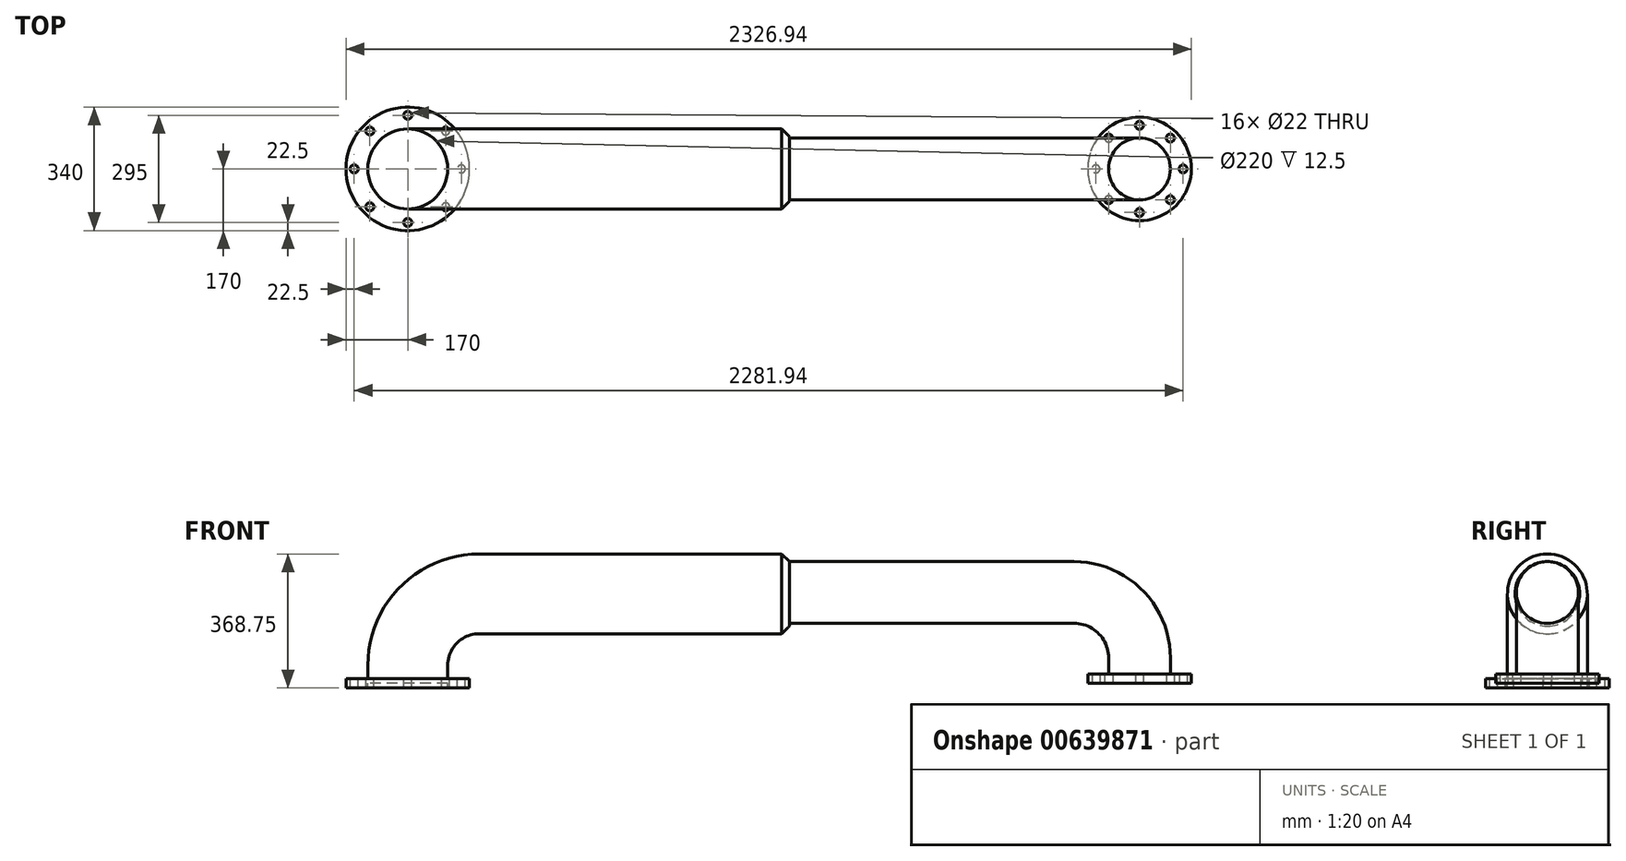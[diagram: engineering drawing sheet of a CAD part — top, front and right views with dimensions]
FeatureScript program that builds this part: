
annotation { "Feature Type Name" : "Feature", "Feature Type Description" : "" }
export const myFeature = defineFeature(function(context is Context, id is Id, definition is map)
    precondition{}
    {
        {
            var Q0;
            Q0=qCreatedBy(makeId("Top.planeOp"),FACE);
            var sketch = newSketch(context, id + "F0", { "sketchPlane" : qUnion([Q0])});
            skCircle(sketch, "E0", {"center": v(0, 0) * mm, "radius": 85 * mm});
            skSolve(sketch);
        }
        {
            var Q0;
            Q0=qCreatedBy(makeId("Front.planeOp"),FACE);
            var sketch = newSketch(context, id + "F1", { "sketchPlane" : qUnion([Q0])});
            skLineSegment(sketch, "E1", {"start": v(0, 0) * mm, "end": v(0, 70) * mm});
            skLineSegment(sketch, "E2", {"start": v(-180, 250) * mm, "end": v(-1000, 250) * mm});
            skPoint(sketch, "E3.visualSharp", {"position": v(0, 250) * mm});
            skArc(sketch, "E3.filletArc", {"start": v(0, 70) * mm, "mid": v(-52.72, 197.28) * mm, "end": v(-180, 250) * mm});
            skSolve(sketch);
        }
        {
            var Q0;
            Q0=makeQuery(id+"F0.imprint","IMPRINT",FACE,{"disambiguationData":[TD([[makeQuery(id+"F0.imprint","IMPRINT",EDGE,{"derivedFrom":sQuery(id+"F0.wireOp",EDGE,"E0")}),1.0]])]});
            var Q1;
            Q1=sQuery(id+"F1.wireOp",EDGE,"E1");
            var Q2;
            Q2=sQuery(id+"F1.wireOp",EDGE,"E3.filletArc");
            var Q3;
            Q3=sQuery(id+"F1.wireOp",EDGE,"E2");
            sweep(context, id + "F2", {"profiles" : qUnion([Q0]), "path" : qUnion([Q1, Q2, Q3])});
        }
        {
            var Q0;
            Q0=makeQuery(id+"F2.opSweep","CAP_FACE",FACE,{"disambiguationData":[OSD([sQuery(id+"F0.wireOp",EDGE,"E0"),sQuery(id+"F1.wireOp",VERTEX,"E1.start")])],"isStart":true});
            var sketch = newSketch(context, id + "F3", { "sketchPlane" : qUnion([Q0])});
            skCircle(sketch, "E4", {"center": v(0, 0) * mm, "radius": 142.5 * mm});
            skCircle(sketch, "E5", {"center": v(0, 120) * mm, "radius": 11 * mm});
            skCircle(sketch, "E6.1.0", {"center": v(-84.85, 84.85) * mm, "radius": 11 * mm});
            skCircle(sketch, "E6.2.0", {"center": v(-120, 0) * mm, "radius": 11 * mm});
            skCircle(sketch, "E6.3.0", {"center": v(-84.85, -84.85) * mm, "radius": 11 * mm});
            skCircle(sketch, "E6.4.0", {"center": v(0, -120) * mm, "radius": 11 * mm});
            skCircle(sketch, "E6.5.0", {"center": v(84.85, -84.85) * mm, "radius": 11 * mm});
            skCircle(sketch, "E6.6.0", {"center": v(120, 0) * mm, "radius": 11 * mm});
            skCircle(sketch, "E6.7.0", {"center": v(84.85, 84.85) * mm, "radius": 11 * mm});
            skSolve(sketch);
        }
        {
            var Q0;
            Q0=makeQuery(id+"F3.imprint","IMPRINT",FACE,{"disambiguationData":[TD([[makeQuery(id+"F3.imprint","IMPRINT",EDGE,{"derivedFrom":sQuery(id+"F3.wireOp",EDGE,"E4")}),1.0]])]});
            extrude(context, id + "F4", {"entities" : qUnion([Q0]), "operationType" : NewBodyOperationType.ADD, "oppositeDirection" : true, "depth" : 25 * mm, "offsetDistance" : 25 * mm});
        }
        {
            var Q0;
            Q0=qCreatedBy(makeId("Top.planeOp"),FACE);
            var sketch = newSketch(context, id + "F5", { "sketchPlane" : qUnion([Q0])});
            skCircle(sketch, "E7", {"center": v(-2014.44, 0) * mm, "radius": 110 * mm});
            skSolve(sketch);
        }
        {
            var Q0;
            Q0=qCreatedBy(makeId("Front.planeOp"),FACE);
            var sketch = newSketch(context, id + "F6", { "sketchPlane" : qUnion([Q0])});
            skLineSegment(sketch, "E8", {"start": v(-2018.2, 0) * mm, "end": v(-2018.2, 50) * mm});
            skLineSegment(sketch, "E9", {"start": v(-1818.2, 250) * mm, "end": v(-964.04, 250) * mm});
            skPoint(sketch, "E10.visualSharp", {"position": v(-2018.2, 250) * mm});
            skArc(sketch, "E10.filletArc", {"start": v(-1818.2, 250) * mm, "mid": v(-1959.61, 191.42) * mm, "end": v(-2018.2, 50) * mm});
            skSolve(sketch);
        }
        {
            var Q0;
            Q0=makeQuery(id+"F5.imprint","IMPRINT",FACE,{"disambiguationData":[TD([[makeQuery(id+"F5.imprint","IMPRINT",EDGE,{"derivedFrom":sQuery(id+"F5.wireOp",EDGE,"E7")}),1.0]])]});
            var Q1;
            Q1=sQuery(id+"F6.wireOp",EDGE,"E8");
            var Q2;
            Q2=sQuery(id+"F6.wireOp",EDGE,"E10.filletArc");
            var Q3;
            Q3=sQuery(id+"F6.wireOp",EDGE,"E9");
            sweep(context, id + "F7", {"operationType" : NewBodyOperationType.ADD, "profiles" : qUnion([Q0]), "path" : qUnion([Q1, Q2, Q3])});
        }
        {
            var Q0;
            Q0=makeQuery(id+"F7.opSweep","CAP_EDGE",EDGE,{"disambiguationData":[OSD([sQuery(id+"F5.wireOp",EDGE,"E7"),sQuery(id+"F6.wireOp",VERTEX,"E9.end")])],"isStart":false});
            chamfer(context, id + "F8", {"entities" : qUnion([Q0]), "width" : 21 * mm, "tangentPropagation" : true});
        }
        {
            var Q0;
            Q0=makeQuery(id+"F7.opSweep","CAP_FACE",FACE,{"disambiguationData":[OSD([sQuery(id+"F5.wireOp",EDGE,"E7"),sQuery(id+"F6.wireOp",VERTEX,"E8.start")])],"isStart":true});
            var sketch = newSketch(context, id + "F9", { "sketchPlane" : qUnion([Q0])});
            skCircle(sketch, "E11", {"center": v(-2014.44, 0) * mm, "radius": 170 * mm});
            skCircle(sketch, "E12", {"center": v(-2014.44, 147.5) * mm, "radius": 11 * mm});
            skCircle(sketch, "E13.1.0", {"center": v(-2118.74, 104.3) * mm, "radius": 11 * mm});
            skCircle(sketch, "E13.2.0", {"center": v(-2161.94, 0) * mm, "radius": 11 * mm});
            skCircle(sketch, "E13.3.0", {"center": v(-2118.74, -104.3) * mm, "radius": 11 * mm});
            skCircle(sketch, "E13.4.0", {"center": v(-2014.44, -147.5) * mm, "radius": 11 * mm});
            skCircle(sketch, "E13.5.0", {"center": v(-1910.14, -104.3) * mm, "radius": 11 * mm});
            skCircle(sketch, "E13.6.0", {"center": v(-1866.94, 0) * mm, "radius": 11 * mm});
            skCircle(sketch, "E13.7.0", {"center": v(-1910.14, 104.3) * mm, "radius": 11 * mm});
            skSolve(sketch);
        }
        {
            var Q0;
            Q0=makeQuery(id+"F9.imprint","IMPRINT",FACE,{"disambiguationData":[TD([[makeQuery(id+"F9.imprint","IMPRINT",EDGE,{"derivedFrom":sQuery(id+"F9.wireOp",EDGE,"E11")}),1.0]])]});
            extrude(context, id + "F10", {"entities" : qUnion([Q0]), "operationType" : NewBodyOperationType.ADD, "endBound" : BoundingType.SYMMETRIC, "depth" : 25 * mm, "offsetDistance" : 25 * mm});
        }
    });
